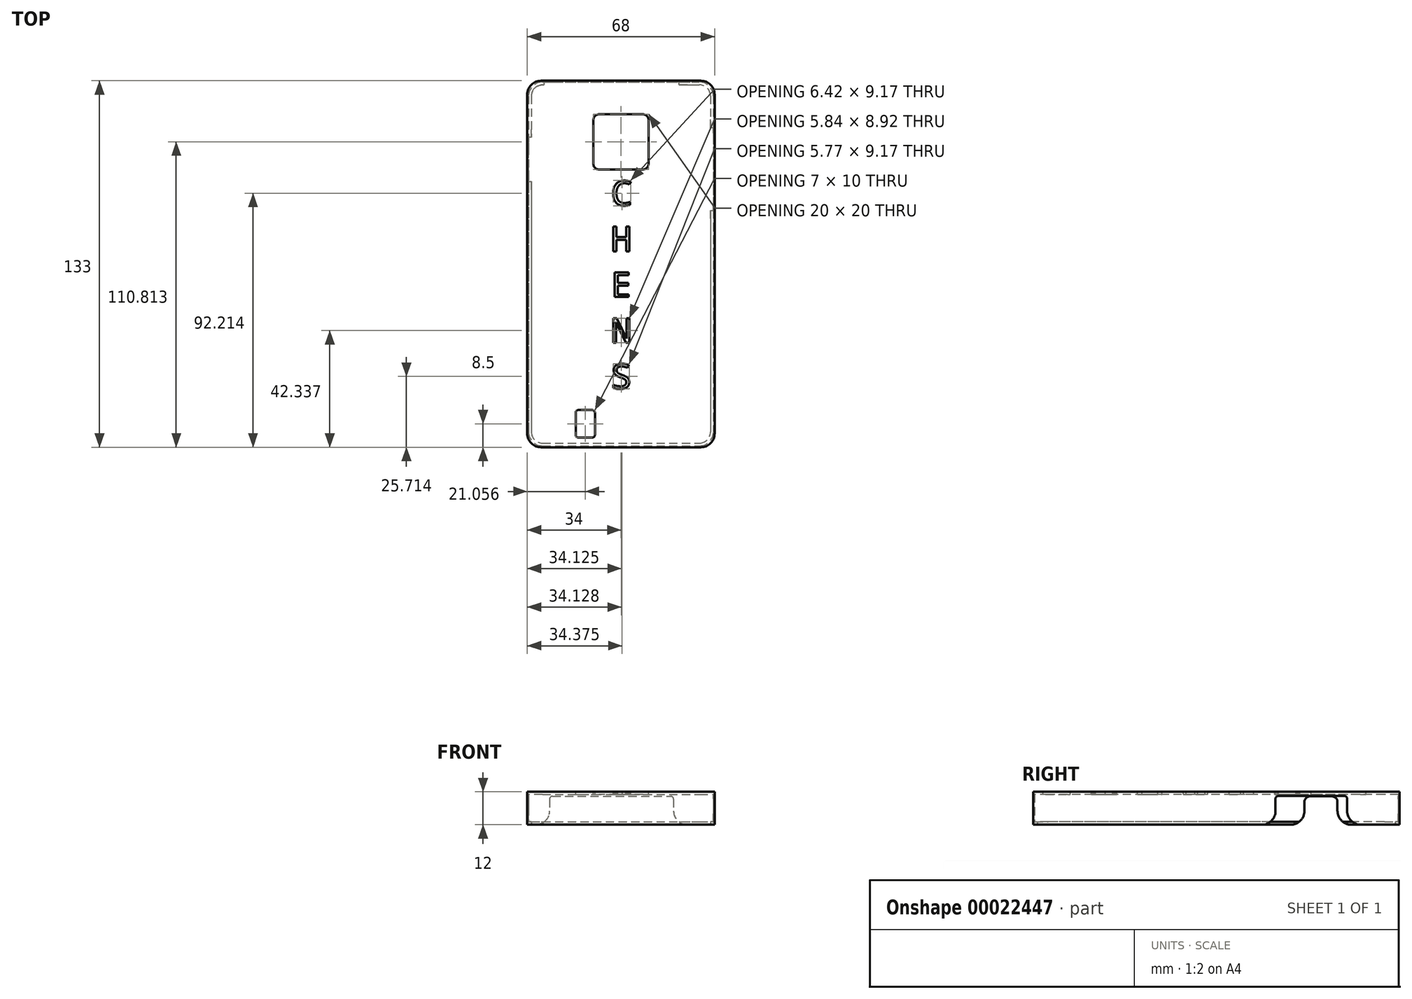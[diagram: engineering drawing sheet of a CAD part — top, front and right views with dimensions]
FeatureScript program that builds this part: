
annotation { "Feature Type Name" : "Feature", "Feature Type Description" : "" }
export const myFeature = defineFeature(function(context is Context, id is Id, definition is map)
    precondition{}
    {
        {
            var Q0;
            Q0=qCreatedBy(makeId("Top.planeOp"),FACE);
            var sketch = newSketch(context, id + "F0", { "sketchPlane" : qUnion([Q0])});
            skLineSegment(sketch, "E0.rect.bottom", {"start": v(29, -66.5) * mm, "end": v(-29, -66.5) * mm});
            skLineSegment(sketch, "E0.rect.top", {"start": v(29, 66.5) * mm, "end": v(-29, 66.5) * mm});
            skLineSegment(sketch, "E0.rect.left", {"start": v(34, -61.5) * mm, "end": v(34, 61.5) * mm});
            skLineSegment(sketch, "E0.rect.right", {"start": v(-34, -61.5) * mm, "end": v(-34, 61.5) * mm});
            skPoint(sketch, "E0.rect.middle", {"position": v(0, 0) * mm});
            skPoint(sketch, "E1.visualSharp", {"position": v(-34, 66.5) * mm});
            skArc(sketch, "E1.filletArc", {"start": v(-29, 66.5) * mm, "mid": v(-32.54, 65.04) * mm, "end": v(-34, 61.5) * mm});
            skPoint(sketch, "E2.visualSharp", {"position": v(-34, -66.5) * mm});
            skArc(sketch, "E2.filletArc", {"start": v(-34, -61.5) * mm, "mid": v(-32.54, -65.04) * mm, "end": v(-29, -66.5) * mm});
            skPoint(sketch, "E3.visualSharp", {"position": v(34, -66.5) * mm});
            skArc(sketch, "E3.filletArc", {"start": v(29, -66.5) * mm, "mid": v(32.54, -65.04) * mm, "end": v(34, -61.5) * mm});
            skPoint(sketch, "E4.visualSharp", {"position": v(34, 66.5) * mm});
            skArc(sketch, "E4.filletArc", {"start": v(34, 61.5) * mm, "mid": v(32.54, 65.04) * mm, "end": v(29, 66.5) * mm});
            skLineSegment(sketch, "E5", {"start": v(0, -66.5) * mm, "end": v(0, 35.5) * mm, "construction": true});
            skLineSegment(sketch, "E6", {"start": v(-34, 44.31) * mm, "end": v(-6.5, 44.31) * mm, "construction": true});
            skLineSegment(sketch, "E7.rect.bottom", {"start": v(8, 54.31) * mm, "end": v(-8, 54.31) * mm});
            skLineSegment(sketch, "E7.rect.top", {"start": v(8, 34.31) * mm, "end": v(-8, 34.31) * mm});
            skLineSegment(sketch, "E7.rect.left", {"start": v(10, 52.31) * mm, "end": v(10, 36.31) * mm});
            skLineSegment(sketch, "E7.rect.right", {"start": v(-10, 52.31) * mm, "end": v(-10, 36.31) * mm});
            skPoint(sketch, "E7.rect.middle", {"position": v(0, 44.31) * mm});
            skPoint(sketch, "E8.visualSharp", {"position": v(-10, 54.31) * mm});
            skArc(sketch, "E8.filletArc", {"start": v(-8, 54.31) * mm, "mid": v(-9.41, 53.73) * mm, "end": v(-10, 52.31) * mm});
            skPoint(sketch, "E9.visualSharp", {"position": v(-10, 34.31) * mm});
            skArc(sketch, "E9.filletArc", {"start": v(-10, 36.31) * mm, "mid": v(-9.41, 34.9) * mm, "end": v(-8, 34.31) * mm});
            skPoint(sketch, "E10.visualSharp", {"position": v(10, 54.31) * mm});
            skArc(sketch, "E10.filletArc", {"start": v(10, 52.31) * mm, "mid": v(9.41, 53.73) * mm, "end": v(8, 54.31) * mm});
            skPoint(sketch, "E11.visualSharp", {"position": v(10, 34.31) * mm});
            skArc(sketch, "E11.filletArc", {"start": v(8, 34.31) * mm, "mid": v(9.41, 34.9) * mm, "end": v(10, 36.31) * mm});
            skLineSegment(sketch, "E12", {"start": v(-34, -58.95) * mm, "end": v(-17, -58.95) * mm, "construction": true});
            skLineSegment(sketch, "E13", {"start": v(-17, -66.5) * mm, "end": v(-17, -63) * mm, "construction": true});
            skLineSegment(sketch, "E14.bottom", {"start": v(-15.44, -63) * mm, "end": v(-10.44, -63) * mm});
            skLineSegment(sketch, "E14.top", {"start": v(-15.44, -53) * mm, "end": v(-10.44, -53) * mm});
            skLineSegment(sketch, "E14.left", {"start": v(-16.44, -62) * mm, "end": v(-16.44, -54) * mm});
            skLineSegment(sketch, "E14.right", {"start": v(-9.44, -62) * mm, "end": v(-9.44, -54) * mm});
            skPoint(sketch, "E15.visualSharp", {"position": v(-16.44, -53) * mm});
            skArc(sketch, "E15.filletArc", {"start": v(-15.44, -53) * mm, "mid": v(-16.15, -53.3) * mm, "end": v(-16.44, -54) * mm});
            skPoint(sketch, "E16.visualSharp", {"position": v(-16.44, -63) * mm});
            skArc(sketch, "E16.filletArc", {"start": v(-16.44, -62) * mm, "mid": v(-16.15, -62.7) * mm, "end": v(-15.44, -63) * mm});
            skPoint(sketch, "E17.visualSharp", {"position": v(-9.44, -53) * mm});
            skArc(sketch, "E17.filletArc", {"start": v(-9.44, -54) * mm, "mid": v(-9.74, -53.3) * mm, "end": v(-10.44, -53) * mm});
            skPoint(sketch, "E18.visualSharp", {"position": v(-9.44, -63) * mm});
            skArc(sketch, "E18.filletArc", {"start": v(-10.44, -63) * mm, "mid": v(-9.74, -62.7) * mm, "end": v(-9.44, -62) * mm});
            skText(sketch, "E19", { "text": "C\nH\nE\nN\nS", "fontName": "DroidSansMono.ttf"});
            const initialGuessF0  = {"E19": [-0.00362, 0.02125, 1, 0, 0.009]};
            skSetInitialGuess(sketch, initialGuessF0);
            skSolve(sketch);
        }
        {
            var Q0;
            Q0 = qSketchRegion(id + "F0", true);
            extrude(context, id + "F1", {"entities" : qUnion([Q0]), "oppositeDirection" : true, "depth" : 11 * mm});
        }
        {
            var Q0;
            Q0=makeQuery(id+"F1.opExtrude","CAP_FACE",FACE,{"disambiguationData":[OSD([sQuery(id+"F0.wireOp",EDGE,"E0.rect.bottom"),sQuery(id+"F0.wireOp",EDGE,"E0.rect.top"),sQuery(id+"F0.wireOp",EDGE,"E0.rect.left"),sQuery(id+"F0.wireOp",EDGE,"E0.rect.right"),sQuery(id+"F0.wireOp",EDGE,"E1.filletArc"),sQuery(id+"F0.wireOp",EDGE,"E2.filletArc"),sQuery(id+"F0.wireOp",EDGE,"E3.filletArc"),sQuery(id+"F0.wireOp",EDGE,"E4.filletArc"),sQuery(id+"F0.wireOp",EDGE,"E7.rect.bottom"),sQuery(id+"F0.wireOp",EDGE,"E7.rect.top"),sQuery(id+"F0.wireOp",EDGE,"E7.rect.left"),sQuery(id+"F0.wireOp",EDGE,"E7.rect.right"),sQuery(id+"F0.wireOp",EDGE,"E8.filletArc"),sQuery(id+"F0.wireOp",EDGE,"E9.filletArc"),sQuery(id+"F0.wireOp",EDGE,"E10.filletArc"),sQuery(id+"F0.wireOp",EDGE,"E11.filletArc"),sQuery(id+"F0.wireOp",EDGE,"E14.bottom"),sQuery(id+"F0.wireOp",EDGE,"E14.top"),sQuery(id+"F0.wireOp",EDGE,"E14.left"),sQuery(id+"F0.wireOp",EDGE,"E14.right"),sQuery(id+"F0.wireOp",EDGE,"E15.filletArc"),sQuery(id+"F0.wireOp",EDGE,"E16.filletArc"),sQuery(id+"F0.wireOp",EDGE,"E17.filletArc"),sQuery(id+"F0.wireOp",EDGE,"E18.filletArc"),sQuery(id+"F0.wireOp",EDGE,"E19.sketch_text.stroke-0"),sQuery(id+"F0.wireOp",EDGE,"E19.sketch_text.stroke-1"),sQuery(id+"F0.wireOp",EDGE,"E19.sketch_text.stroke-2"),sQuery(id+"F0.wireOp",EDGE,"E19.sketch_text.stroke-3"),sQuery(id+"F0.wireOp",EDGE,"E19.sketch_text.stroke-4"),sQuery(id+"F0.wireOp",EDGE,"E19.sketch_text.stroke-5"),sQuery(id+"F0.wireOp",EDGE,"E19.sketch_text.stroke-6"),sQuery(id+"F0.wireOp",EDGE,"E19.sketch_text.stroke-7"),sQuery(id+"F0.wireOp",EDGE,"E19.sketch_text.stroke-8"),sQuery(id+"F0.wireOp",EDGE,"E19.sketch_text.stroke-9"),sQuery(id+"F0.wireOp",EDGE,"E19.sketch_text.stroke-10"),sQuery(id+"F0.wireOp",EDGE,"E19.sketch_text.stroke-11"),sQuery(id+"F0.wireOp",EDGE,"E19.sketch_text.stroke-12"),sQuery(id+"F0.wireOp",EDGE,"E19.sketch_text.stroke-13"),sQuery(id+"F0.wireOp",EDGE,"E19.sketch_text.stroke-14"),sQuery(id+"F0.wireOp",EDGE,"E19.sketch_text.stroke-15"),sQuery(id+"F0.wireOp",EDGE,"E19.sketch_text.stroke-16"),sQuery(id+"F0.wireOp",EDGE,"E19.sketch_text.stroke-17"),sQuery(id+"F0.wireOp",EDGE,"E19.sketch_text.stroke-18"),sQuery(id+"F0.wireOp",EDGE,"E19.sketch_text.stroke-19"),sQuery(id+"F0.wireOp",EDGE,"E19.sketch_text.stroke-20"),sQuery(id+"F0.wireOp",EDGE,"E19.sketch_text.stroke-21"),sQuery(id+"F0.wireOp",EDGE,"E19.sketch_text.stroke-22"),sQuery(id+"F0.wireOp",EDGE,"E19.sketch_text.stroke-23"),sQuery(id+"F0.wireOp",EDGE,"E19.sketch_text.stroke-24"),sQuery(id+"F0.wireOp",EDGE,"E19.sketch_text.stroke-25"),sQuery(id+"F0.wireOp",EDGE,"E19.sketch_text.stroke-26"),sQuery(id+"F0.wireOp",EDGE,"E19.sketch_text.stroke-27"),sQuery(id+"F0.wireOp",EDGE,"E19.sketch_text.stroke-28"),sQuery(id+"F0.wireOp",EDGE,"E19.sketch_text.stroke-29"),sQuery(id+"F0.wireOp",EDGE,"E19.sketch_text.stroke-30"),sQuery(id+"F0.wireOp",EDGE,"E19.sketch_text.stroke-31"),sQuery(id+"F0.wireOp",EDGE,"E19.sketch_text.stroke-32"),sQuery(id+"F0.wireOp",EDGE,"E19.sketch_text.stroke-33"),sQuery(id+"F0.wireOp",EDGE,"E19.sketch_text.stroke-34"),sQuery(id+"F0.wireOp",EDGE,"E19.sketch_text.stroke-35"),sQuery(id+"F0.wireOp",EDGE,"E19.sketch_text.stroke-36"),sQuery(id+"F0.wireOp",EDGE,"E19.sketch_text.stroke-37"),sQuery(id+"F0.wireOp",EDGE,"E19.sketch_text.stroke-38"),sQuery(id+"F0.wireOp",EDGE,"E19.sketch_text.stroke-39"),sQuery(id+"F0.wireOp",EDGE,"E19.sketch_text.stroke-40"),sQuery(id+"F0.wireOp",EDGE,"E19.sketch_text.stroke-41"),sQuery(id+"F0.wireOp",EDGE,"E19.sketch_text.stroke-42"),sQuery(id+"F0.wireOp",EDGE,"E19.sketch_text.stroke-43"),sQuery(id+"F0.wireOp",EDGE,"E19.sketch_text.stroke-44"),sQuery(id+"F0.wireOp",EDGE,"E19.sketch_text.stroke-45"),sQuery(id+"F0.wireOp",EDGE,"E19.sketch_text.stroke-46"),sQuery(id+"F0.wireOp",EDGE,"E19.sketch_text.stroke-47"),sQuery(id+"F0.wireOp",EDGE,"E19.sketch_text.stroke-48"),sQuery(id+"F0.wireOp",EDGE,"E19.sketch_text.stroke-49"),sQuery(id+"F0.wireOp",EDGE,"E19.sketch_text.stroke-50"),sQuery(id+"F0.wireOp",EDGE,"E19.sketch_text.stroke-51"),sQuery(id+"F0.wireOp",EDGE,"E19.sketch_text.stroke-52"),sQuery(id+"F0.wireOp",EDGE,"E19.sketch_text.stroke-53"),sQuery(id+"F0.wireOp",EDGE,"E19.sketch_text.stroke-54"),sQuery(id+"F0.wireOp",EDGE,"E19.sketch_text.stroke-55"),sQuery(id+"F0.wireOp",EDGE,"E19.sketch_text.stroke-56"),sQuery(id+"F0.wireOp",EDGE,"E19.sketch_text.stroke-57"),sQuery(id+"F0.wireOp",EDGE,"E19.sketch_text.stroke-58"),sQuery(id+"F0.wireOp",EDGE,"E19.sketch_text.stroke-59"),sQuery(id+"F0.wireOp",EDGE,"E19.sketch_text.stroke-60"),sQuery(id+"F0.wireOp",EDGE,"E19.sketch_text.stroke-61"),sQuery(id+"F0.wireOp",EDGE,"E19.sketch_text.stroke-62"),sQuery(id+"F0.wireOp",EDGE,"E19.sketch_text.stroke-63"),sQuery(id+"F0.wireOp",EDGE,"E19.sketch_text.stroke-64"),sQuery(id+"F0.wireOp",EDGE,"E19.sketch_text.stroke-65"),sQuery(id+"F0.wireOp",EDGE,"E19.sketch_text.stroke-66"),sQuery(id+"F0.wireOp",EDGE,"E19.sketch_text.stroke-67"),sQuery(id+"F0.wireOp",EDGE,"E19.sketch_text.stroke-68"),sQuery(id+"F0.wireOp",EDGE,"E19.sketch_text.stroke-69"),sQuery(id+"F0.wireOp",EDGE,"E19.sketch_text.stroke-70"),sQuery(id+"F0.wireOp",EDGE,"E19.sketch_text.stroke-71")])],"isStart":false});
            var sketch = newSketch(context, id + "F2", { "sketchPlane" : qUnion([Q0])});
            skLineSegment(sketch, "E20.rect.bottom", {"start": v(-28.5, -66) * mm, "end": v(28.5, -66) * mm});
            skLineSegment(sketch, "E20.rect.top", {"start": v(-28.5, 66) * mm, "end": v(28.5, 66) * mm});
            skLineSegment(sketch, "E20.rect.left", {"start": v(-33.5, -61) * mm, "end": v(-33.5, 61) * mm});
            skLineSegment(sketch, "E20.rect.right", {"start": v(33.5, -61) * mm, "end": v(33.5, 61) * mm});
            skPoint(sketch, "E20.rect.middle", {"position": v(0, 0) * mm});
            skPoint(sketch, "E21.visualSharp", {"position": v(-33.5, -66) * mm});
            skArc(sketch, "E21.filletArc", {"start": v(-33.5, -61) * mm, "mid": v(-32.04, -64.54) * mm, "end": v(-28.5, -66) * mm});
            skPoint(sketch, "E22.visualSharp", {"position": v(33.5, -66) * mm});
            skArc(sketch, "E22.filletArc", {"start": v(28.5, -66) * mm, "mid": v(32.04, -64.54) * mm, "end": v(33.5, -61) * mm});
            skPoint(sketch, "E23.visualSharp", {"position": v(33.5, 66) * mm});
            skArc(sketch, "E23.filletArc", {"start": v(33.5, 61) * mm, "mid": v(32.04, 64.54) * mm, "end": v(28.5, 66) * mm});
            skPoint(sketch, "E24.visualSharp", {"position": v(-33.5, 66) * mm});
            skArc(sketch, "E24.filletArc", {"start": v(-28.5, 66) * mm, "mid": v(-32.04, 64.54) * mm, "end": v(-33.5, 61) * mm});
            skSolve(sketch);
        }
        {
            var Q0;
            Q0 = qSketchRegion(id + "F2", true);
            extrude(context, id + "F3", {"entities" : qUnion([Q0]), "operationType" : NewBodyOperationType.REMOVE, "oppositeDirection" : true, "depth" : 10 * mm});
        }
        {
            var Q0;
            Q0=makeQuery(id+"F1.opExtrude","CAP_FACE",FACE,{"disambiguationData":[OSD([sQuery(id+"F0.wireOp",EDGE,"E0.rect.bottom"),sQuery(id+"F0.wireOp",EDGE,"E0.rect.top"),sQuery(id+"F0.wireOp",EDGE,"E0.rect.left"),sQuery(id+"F0.wireOp",EDGE,"E0.rect.right"),sQuery(id+"F0.wireOp",EDGE,"E1.filletArc"),sQuery(id+"F0.wireOp",EDGE,"E2.filletArc"),sQuery(id+"F0.wireOp",EDGE,"E3.filletArc"),sQuery(id+"F0.wireOp",EDGE,"E4.filletArc"),sQuery(id+"F0.wireOp",EDGE,"E7.rect.bottom"),sQuery(id+"F0.wireOp",EDGE,"E7.rect.top"),sQuery(id+"F0.wireOp",EDGE,"E7.rect.left"),sQuery(id+"F0.wireOp",EDGE,"E7.rect.right"),sQuery(id+"F0.wireOp",EDGE,"E8.filletArc"),sQuery(id+"F0.wireOp",EDGE,"E9.filletArc"),sQuery(id+"F0.wireOp",EDGE,"E10.filletArc"),sQuery(id+"F0.wireOp",EDGE,"E11.filletArc"),sQuery(id+"F0.wireOp",EDGE,"E14.bottom"),sQuery(id+"F0.wireOp",EDGE,"E14.top"),sQuery(id+"F0.wireOp",EDGE,"E14.left"),sQuery(id+"F0.wireOp",EDGE,"E14.right"),sQuery(id+"F0.wireOp",EDGE,"E15.filletArc"),sQuery(id+"F0.wireOp",EDGE,"E16.filletArc"),sQuery(id+"F0.wireOp",EDGE,"E17.filletArc"),sQuery(id+"F0.wireOp",EDGE,"E18.filletArc"),sQuery(id+"F0.wireOp",EDGE,"E19.sketch_text.stroke-0"),sQuery(id+"F0.wireOp",EDGE,"E19.sketch_text.stroke-1"),sQuery(id+"F0.wireOp",EDGE,"E19.sketch_text.stroke-2"),sQuery(id+"F0.wireOp",EDGE,"E19.sketch_text.stroke-3"),sQuery(id+"F0.wireOp",EDGE,"E19.sketch_text.stroke-4"),sQuery(id+"F0.wireOp",EDGE,"E19.sketch_text.stroke-5"),sQuery(id+"F0.wireOp",EDGE,"E19.sketch_text.stroke-6"),sQuery(id+"F0.wireOp",EDGE,"E19.sketch_text.stroke-7"),sQuery(id+"F0.wireOp",EDGE,"E19.sketch_text.stroke-8"),sQuery(id+"F0.wireOp",EDGE,"E19.sketch_text.stroke-9"),sQuery(id+"F0.wireOp",EDGE,"E19.sketch_text.stroke-10"),sQuery(id+"F0.wireOp",EDGE,"E19.sketch_text.stroke-11"),sQuery(id+"F0.wireOp",EDGE,"E19.sketch_text.stroke-12"),sQuery(id+"F0.wireOp",EDGE,"E19.sketch_text.stroke-13"),sQuery(id+"F0.wireOp",EDGE,"E19.sketch_text.stroke-14"),sQuery(id+"F0.wireOp",EDGE,"E19.sketch_text.stroke-15"),sQuery(id+"F0.wireOp",EDGE,"E19.sketch_text.stroke-16"),sQuery(id+"F0.wireOp",EDGE,"E19.sketch_text.stroke-17"),sQuery(id+"F0.wireOp",EDGE,"E19.sketch_text.stroke-18"),sQuery(id+"F0.wireOp",EDGE,"E19.sketch_text.stroke-19"),sQuery(id+"F0.wireOp",EDGE,"E19.sketch_text.stroke-20"),sQuery(id+"F0.wireOp",EDGE,"E19.sketch_text.stroke-21"),sQuery(id+"F0.wireOp",EDGE,"E19.sketch_text.stroke-22"),sQuery(id+"F0.wireOp",EDGE,"E19.sketch_text.stroke-23"),sQuery(id+"F0.wireOp",EDGE,"E19.sketch_text.stroke-24"),sQuery(id+"F0.wireOp",EDGE,"E19.sketch_text.stroke-25"),sQuery(id+"F0.wireOp",EDGE,"E19.sketch_text.stroke-26"),sQuery(id+"F0.wireOp",EDGE,"E19.sketch_text.stroke-27"),sQuery(id+"F0.wireOp",EDGE,"E19.sketch_text.stroke-28"),sQuery(id+"F0.wireOp",EDGE,"E19.sketch_text.stroke-29"),sQuery(id+"F0.wireOp",EDGE,"E19.sketch_text.stroke-30"),sQuery(id+"F0.wireOp",EDGE,"E19.sketch_text.stroke-31"),sQuery(id+"F0.wireOp",EDGE,"E19.sketch_text.stroke-32"),sQuery(id+"F0.wireOp",EDGE,"E19.sketch_text.stroke-33"),sQuery(id+"F0.wireOp",EDGE,"E19.sketch_text.stroke-34"),sQuery(id+"F0.wireOp",EDGE,"E19.sketch_text.stroke-35"),sQuery(id+"F0.wireOp",EDGE,"E19.sketch_text.stroke-36"),sQuery(id+"F0.wireOp",EDGE,"E19.sketch_text.stroke-37"),sQuery(id+"F0.wireOp",EDGE,"E19.sketch_text.stroke-38"),sQuery(id+"F0.wireOp",EDGE,"E19.sketch_text.stroke-39"),sQuery(id+"F0.wireOp",EDGE,"E19.sketch_text.stroke-40"),sQuery(id+"F0.wireOp",EDGE,"E19.sketch_text.stroke-41"),sQuery(id+"F0.wireOp",EDGE,"E19.sketch_text.stroke-42"),sQuery(id+"F0.wireOp",EDGE,"E19.sketch_text.stroke-43"),sQuery(id+"F0.wireOp",EDGE,"E19.sketch_text.stroke-44"),sQuery(id+"F0.wireOp",EDGE,"E19.sketch_text.stroke-45"),sQuery(id+"F0.wireOp",EDGE,"E19.sketch_text.stroke-46"),sQuery(id+"F0.wireOp",EDGE,"E19.sketch_text.stroke-47"),sQuery(id+"F0.wireOp",EDGE,"E19.sketch_text.stroke-48"),sQuery(id+"F0.wireOp",EDGE,"E19.sketch_text.stroke-49"),sQuery(id+"F0.wireOp",EDGE,"E19.sketch_text.stroke-50"),sQuery(id+"F0.wireOp",EDGE,"E19.sketch_text.stroke-51"),sQuery(id+"F0.wireOp",EDGE,"E19.sketch_text.stroke-52"),sQuery(id+"F0.wireOp",EDGE,"E19.sketch_text.stroke-53"),sQuery(id+"F0.wireOp",EDGE,"E19.sketch_text.stroke-54"),sQuery(id+"F0.wireOp",EDGE,"E19.sketch_text.stroke-55"),sQuery(id+"F0.wireOp",EDGE,"E19.sketch_text.stroke-56"),sQuery(id+"F0.wireOp",EDGE,"E19.sketch_text.stroke-57"),sQuery(id+"F0.wireOp",EDGE,"E19.sketch_text.stroke-58"),sQuery(id+"F0.wireOp",EDGE,"E19.sketch_text.stroke-59"),sQuery(id+"F0.wireOp",EDGE,"E19.sketch_text.stroke-60"),sQuery(id+"F0.wireOp",EDGE,"E19.sketch_text.stroke-61"),sQuery(id+"F0.wireOp",EDGE,"E19.sketch_text.stroke-62"),sQuery(id+"F0.wireOp",EDGE,"E19.sketch_text.stroke-63"),sQuery(id+"F0.wireOp",EDGE,"E19.sketch_text.stroke-64"),sQuery(id+"F0.wireOp",EDGE,"E19.sketch_text.stroke-65"),sQuery(id+"F0.wireOp",EDGE,"E19.sketch_text.stroke-66"),sQuery(id+"F0.wireOp",EDGE,"E19.sketch_text.stroke-67"),sQuery(id+"F0.wireOp",EDGE,"E19.sketch_text.stroke-68"),sQuery(id+"F0.wireOp",EDGE,"E19.sketch_text.stroke-69"),sQuery(id+"F0.wireOp",EDGE,"E19.sketch_text.stroke-70"),sQuery(id+"F0.wireOp",EDGE,"E19.sketch_text.stroke-71")])],"isStart":false});
            var sketch = newSketch(context, id + "F4", { "sketchPlane" : qUnion([Q0])});
            skLineSegment(sketch, "E25.rect.bottom", {"start": v(-29, -66.5) * mm, "end": v(29, -66.5) * mm});
            skLineSegment(sketch, "E25.rect.top", {"start": v(-29, 66.5) * mm, "end": v(29, 66.5) * mm});
            skLineSegment(sketch, "E25.rect.left", {"start": v(-34, -61.5) * mm, "end": v(-34, 61.5) * mm});
            skLineSegment(sketch, "E25.rect.right", {"start": v(34, -61.5) * mm, "end": v(34, 61.5) * mm});
            skPoint(sketch, "E25.rect.middle", {"position": v(0, 0) * mm});
            skPoint(sketch, "E26.visualSharp", {"position": v(-34, -66.5) * mm});
            skArc(sketch, "E26.filletArc", {"start": v(-34, -61.5) * mm, "mid": v(-32.54, -65.04) * mm, "end": v(-29, -66.5) * mm});
            skPoint(sketch, "E27.visualSharp", {"position": v(34, -66.5) * mm});
            skArc(sketch, "E27.filletArc", {"start": v(29, -66.5) * mm, "mid": v(32.54, -65.04) * mm, "end": v(34, -61.5) * mm});
            skPoint(sketch, "E28.visualSharp", {"position": v(34, 66.5) * mm});
            skArc(sketch, "E28.filletArc", {"start": v(34, 61.5) * mm, "mid": v(32.54, 65.04) * mm, "end": v(29, 66.5) * mm});
            skPoint(sketch, "E29.visualSharp", {"position": v(-34, 66.5) * mm});
            skArc(sketch, "E29.filletArc", {"start": v(-29, 66.5) * mm, "mid": v(-32.54, 65.04) * mm, "end": v(-34, 61.5) * mm});
            skSolve(sketch);
        }
        {
            var Q0;
            Q0 = qSketchRegion(id + "F4", true);
            extrude(context, id + "F5", {"entities" : qUnion([Q0]), "operationType" : NewBodyOperationType.ADD, "depth" : 1 * mm});
        }
        {
            var Q0;
            Q0=makeQuery(id+"F5.opExtrude","CAP_FACE",FACE,{"disambiguationData":[OSD([sQuery(id+"F4.wireOp",EDGE,"E25.rect.bottom"),sQuery(id+"F4.wireOp",EDGE,"E25.rect.top"),sQuery(id+"F4.wireOp",EDGE,"E25.rect.left"),sQuery(id+"F4.wireOp",EDGE,"E25.rect.right"),sQuery(id+"F4.wireOp",EDGE,"E26.filletArc"),sQuery(id+"F4.wireOp",EDGE,"E27.filletArc"),sQuery(id+"F4.wireOp",EDGE,"E28.filletArc"),sQuery(id+"F4.wireOp",EDGE,"E29.filletArc")])],"isStart":false});
            var sketch = newSketch(context, id + "F6", { "sketchPlane" : qUnion([Q0])});
            skLineSegment(sketch, "E30.rect.bottom", {"start": v(-28.5, -65) * mm, "end": v(28.5, -65) * mm});
            skLineSegment(sketch, "E30.rect.top", {"start": v(-28.5, 65) * mm, "end": v(28.5, 65) * mm});
            skLineSegment(sketch, "E30.rect.left", {"start": v(-32.5, -61) * mm, "end": v(-32.5, 61) * mm});
            skLineSegment(sketch, "E30.rect.right", {"start": v(32.5, -61) * mm, "end": v(32.5, 61) * mm});
            skPoint(sketch, "E30.rect.middle", {"position": v(0, 0) * mm});
            skPoint(sketch, "E31.visualSharp", {"position": v(-32.5, -65) * mm});
            skArc(sketch, "E31.filletArc", {"start": v(-32.5, -61) * mm, "mid": v(-31.33, -63.83) * mm, "end": v(-28.5, -65) * mm});
            skPoint(sketch, "E32.visualSharp", {"position": v(32.5, -65) * mm});
            skArc(sketch, "E32.filletArc", {"start": v(28.5, -65) * mm, "mid": v(31.33, -63.83) * mm, "end": v(32.5, -61) * mm});
            skPoint(sketch, "E33.visualSharp", {"position": v(32.5, 65) * mm});
            skArc(sketch, "E33.filletArc", {"start": v(32.5, 61) * mm, "mid": v(31.33, 63.83) * mm, "end": v(28.5, 65) * mm});
            skPoint(sketch, "E34.visualSharp", {"position": v(-32.5, 65) * mm});
            skArc(sketch, "E34.filletArc", {"start": v(-28.5, 65) * mm, "mid": v(-31.33, 63.83) * mm, "end": v(-32.5, 61) * mm});
            skSolve(sketch);
        }
        {
            var Q0;
            Q0 = qSketchRegion(id + "F6", true);
            extrude(context, id + "F7", {"entities" : qUnion([Q0]), "operationType" : NewBodyOperationType.REMOVE, "oppositeDirection" : true, "depth" : 1 * mm});
        }
        {
            var Q0;
            Q0=makeQuery(id+"F5.boolean.opBoolean","MERGE",FACE,{"derivedFrom":[makeQuery(id+"F1.opExtrude","SWEPT_FACE",FACE,{"disambiguationData":[OSD([sQuery(id+"F0.wireOp",EDGE,"E0.rect.right")])]}),makeQuery(id+"F5.opExtrude","SWEPT_FACE",FACE,{"disambiguationData":[OSD([sQuery(id+"F4.wireOp",EDGE,"E25.rect.left")])]})]});
            var sketch = newSketch(context, id + "F8", { "sketchPlane" : qUnion([Q0])});
            skPoint(sketch, "E35", {"position": v(-61.5, -12) * mm});
            skLineSegment(sketch, "E36", {"start": v(-61.5, -12) * mm, "end": v(-66.53, -12) * mm, "construction": true});
            skLineSegment(sketch, "E37", {"start": v(-66.53, -12) * mm, "end": v(-66.53, -8.37) * mm, "construction": true});
            skLineSegment(sketch, "E38", {"start": v(-66.53, -8.37) * mm, "end": v(-42.53, -8.37) * mm, "construction": true});
            skLineSegment(sketch, "E39", {"start": v(-42.7, -5.25) * mm, "end": v(-33.7, -5.25) * mm, "construction": true});
            skLineSegment(sketch, "E40.bottom", {"start": v(-43.93, -13.2) * mm, "end": v(-31.93, -13.2) * mm});
            skLineSegment(sketch, "E40.top", {"start": v(-41.93, -1.72) * mm, "end": v(-33.93, -1.72) * mm});
            skLineSegment(sketch, "E40.left", {"start": v(-43.93, -13.2) * mm, "end": v(-43.93, -3.72) * mm});
            skLineSegment(sketch, "E40.right", {"start": v(-31.93, -13.2) * mm, "end": v(-31.93, -3.72) * mm});
            skPoint(sketch, "E41.visualSharp", {"position": v(-43.93, -1.72) * mm});
            skArc(sketch, "E41.filletArc", {"start": v(-41.93, -1.72) * mm, "mid": v(-43.34, -2.3) * mm, "end": v(-43.93, -3.72) * mm});
            skPoint(sketch, "E42.visualSharp", {"position": v(-31.93, -1.72) * mm});
            skArc(sketch, "E42.filletArc", {"start": v(-31.93, -3.72) * mm, "mid": v(-32.51, -2.3) * mm, "end": v(-33.93, -1.72) * mm});
            skSolve(sketch);
        }
        {
            var Q0;
            Q0 = qSketchRegion(id + "F8", true);
            extrude(context, id + "F9", {"entities" : qUnion([Q0]), "operationType" : NewBodyOperationType.REMOVE, "oppositeDirection" : true, "depth" : 2 * mm});
        }
        {
            var Q0;
            Q0=makeQuery(id+"F9.boolean.opBoolean","INTERSECT",EDGE,{"derivedFrom":[makeQuery(id+"F5.opExtrude","CAP_FACE",FACE,{"disambiguationData":[OSD([sQuery(id+"F4.wireOp",EDGE,"E25.rect.bottom"),sQuery(id+"F4.wireOp",EDGE,"E25.rect.top"),sQuery(id+"F4.wireOp",EDGE,"E25.rect.left"),sQuery(id+"F4.wireOp",EDGE,"E25.rect.right"),sQuery(id+"F4.wireOp",EDGE,"E26.filletArc"),sQuery(id+"F4.wireOp",EDGE,"E27.filletArc"),sQuery(id+"F4.wireOp",EDGE,"E28.filletArc"),sQuery(id+"F4.wireOp",EDGE,"E29.filletArc")])],"isStart":false}),makeQuery(id+"F9.opExtrude","SWEPT_FACE",FACE,{"disambiguationData":[OSD([sQuery(id+"F8.wireOp",EDGE,"E40.left")])]})]});
            var Q1;
            Q1=makeQuery(id+"F9.boolean.opBoolean","INTERSECT",EDGE,{"derivedFrom":[makeQuery(id+"F5.opExtrude","CAP_FACE",FACE,{"disambiguationData":[OSD([sQuery(id+"F4.wireOp",EDGE,"E25.rect.bottom"),sQuery(id+"F4.wireOp",EDGE,"E25.rect.top"),sQuery(id+"F4.wireOp",EDGE,"E25.rect.left"),sQuery(id+"F4.wireOp",EDGE,"E25.rect.right"),sQuery(id+"F4.wireOp",EDGE,"E26.filletArc"),sQuery(id+"F4.wireOp",EDGE,"E27.filletArc"),sQuery(id+"F4.wireOp",EDGE,"E28.filletArc"),sQuery(id+"F4.wireOp",EDGE,"E29.filletArc")])],"isStart":false}),makeQuery(id+"F9.opExtrude","SWEPT_FACE",FACE,{"disambiguationData":[OSD([sQuery(id+"F8.wireOp",EDGE,"E40.right")])]})]});
            fillet(context, id + "F10", {"entities" : qUnion([Q0, Q1]), "radius" : 5 * mm, "tangentPropagation" : true, "allowEdgeOverflow" : false});
        }
        {
            var Q0;
            Q0=makeQuery(id+"F5.boolean.opBoolean","MERGE",FACE,{"derivedFrom":[makeQuery(id+"F1.opExtrude","SWEPT_FACE",FACE,{"disambiguationData":[OSD([sQuery(id+"F0.wireOp",EDGE,"E0.rect.left")])]}),makeQuery(id+"F5.opExtrude","SWEPT_FACE",FACE,{"disambiguationData":[OSD([sQuery(id+"F4.wireOp",EDGE,"E25.rect.right")])]})]});
            var sketch = newSketch(context, id + "F11", { "sketchPlane" : qUnion([Q0])});
            skPoint(sketch, "E43", {"position": v(61.5, -6) * mm});
            skLineSegment(sketch, "E44", {"start": v(61.5, -6) * mm, "end": v(66.5, -6) * mm, "construction": true});
            skLineSegment(sketch, "E45", {"start": v(66.5, -6) * mm, "end": v(66.5, -4.15) * mm, "construction": true});
            skLineSegment(sketch, "E46", {"start": v(66.5, -4.15) * mm, "end": v(46.5, -4.15) * mm, "construction": true});
            skLineSegment(sketch, "E47.bottom", {"start": v(46.45, -1.57) * mm, "end": v(22.45, -1.57) * mm});
            skLineSegment(sketch, "E47.top", {"start": v(47.45, -13.62) * mm, "end": v(21.45, -13.62) * mm});
            skLineSegment(sketch, "E47.left", {"start": v(47.45, -2.57) * mm, "end": v(47.45, -13.62) * mm});
            skLineSegment(sketch, "E47.right", {"start": v(21.45, -2.57) * mm, "end": v(21.45, -13.62) * mm});
            skPoint(sketch, "E48.visualSharp", {"position": v(47.45, -1.57) * mm});
            skArc(sketch, "E48.filletArc", {"start": v(47.45, -2.57) * mm, "mid": v(47.16, -1.86) * mm, "end": v(46.45, -1.57) * mm});
            skPoint(sketch, "E49.visualSharp", {"position": v(21.45, -1.57) * mm});
            skArc(sketch, "E49.filletArc", {"start": v(22.45, -1.57) * mm, "mid": v(21.74, -1.86) * mm, "end": v(21.45, -2.57) * mm});
            skSolve(sketch);
        }
        {
            var Q0;
            Q0 = qSketchRegion(id + "F11", true);
            extrude(context, id + "F12", {"entities" : qUnion([Q0]), "operationType" : NewBodyOperationType.REMOVE, "oppositeDirection" : true, "depth" : 2 * mm});
        }
        {
            var Q0;
            Q0=makeQuery(id+"F12.boolean.opBoolean","INTERSECT",EDGE,{"derivedFrom":[makeQuery(id+"F5.opExtrude","CAP_FACE",FACE,{"disambiguationData":[OSD([sQuery(id+"F4.wireOp",EDGE,"E25.rect.bottom"),sQuery(id+"F4.wireOp",EDGE,"E25.rect.top"),sQuery(id+"F4.wireOp",EDGE,"E25.rect.left"),sQuery(id+"F4.wireOp",EDGE,"E25.rect.right"),sQuery(id+"F4.wireOp",EDGE,"E26.filletArc"),sQuery(id+"F4.wireOp",EDGE,"E27.filletArc"),sQuery(id+"F4.wireOp",EDGE,"E28.filletArc"),sQuery(id+"F4.wireOp",EDGE,"E29.filletArc")])],"isStart":false}),makeQuery(id+"F12.opExtrude","SWEPT_FACE",FACE,{"disambiguationData":[OSD([sQuery(id+"F11.wireOp",EDGE,"E47.left")])]})]});
            var Q1;
            Q1=makeQuery(id+"F12.boolean.opBoolean","INTERSECT",EDGE,{"derivedFrom":[makeQuery(id+"F5.opExtrude","CAP_FACE",FACE,{"disambiguationData":[OSD([sQuery(id+"F4.wireOp",EDGE,"E25.rect.bottom"),sQuery(id+"F4.wireOp",EDGE,"E25.rect.top"),sQuery(id+"F4.wireOp",EDGE,"E25.rect.left"),sQuery(id+"F4.wireOp",EDGE,"E25.rect.right"),sQuery(id+"F4.wireOp",EDGE,"E26.filletArc"),sQuery(id+"F4.wireOp",EDGE,"E27.filletArc"),sQuery(id+"F4.wireOp",EDGE,"E28.filletArc"),sQuery(id+"F4.wireOp",EDGE,"E29.filletArc")])],"isStart":false}),makeQuery(id+"F12.opExtrude","SWEPT_FACE",FACE,{"disambiguationData":[OSD([sQuery(id+"F11.wireOp",EDGE,"E47.right")])]})]});
            fillet(context, id + "F13", {"entities" : qUnion([Q0, Q1]), "radius" : 5 * mm, "tangentPropagation" : true, "allowEdgeOverflow" : false});
        }
        {
            var Q0;
            Q0=makeQuery(id+"F5.boolean.opBoolean","MERGE",FACE,{"derivedFrom":[makeQuery(id+"F1.opExtrude","SWEPT_FACE",FACE,{"disambiguationData":[OSD([sQuery(id+"F0.wireOp",EDGE,"E0.rect.top")])]}),makeQuery(id+"F5.opExtrude","SWEPT_FACE",FACE,{"disambiguationData":[OSD([sQuery(id+"F4.wireOp",EDGE,"E25.rect.bottom")])]})]});
            var sketch = newSketch(context, id + "F14", { "sketchPlane" : qUnion([Q0])});
            skPoint(sketch, "E50", {"position": v(-29, -6) * mm});
            skPoint(sketch, "E51", {"position": v(29, -6) * mm});
            skLineSegment(sketch, "E52", {"start": v(29, -6) * mm, "end": v(34, -6.08) * mm, "construction": true});
            skLineSegment(sketch, "E53", {"start": v(34, -6.08) * mm, "end": v(34, -7.9) * mm, "construction": true});
            skLineSegment(sketch, "E54", {"start": v(34, -7.9) * mm, "end": v(25.5, -7.9) * mm, "construction": true});
            skLineSegment(sketch, "E55", {"start": v(-29, -6) * mm, "end": v(-34, -6) * mm, "construction": true});
            skLineSegment(sketch, "E56", {"start": v(-34, -6) * mm, "end": v(-34, -8.67) * mm, "construction": true});
            skLineSegment(sketch, "E57", {"start": v(-34, -8.67) * mm, "end": v(-18.5, -8.67) * mm, "construction": true});
            skLineSegment(sketch, "E58.bottom", {"start": v(24.9, -1.7) * mm, "end": v(-18.1, -1.7) * mm});
            skLineSegment(sketch, "E58.top", {"start": v(25.9, -12.7) * mm, "end": v(-19.1, -12.7) * mm});
            skLineSegment(sketch, "E58.left", {"start": v(25.9, -2.7) * mm, "end": v(25.9, -12.7) * mm});
            skLineSegment(sketch, "E58.right", {"start": v(-19.1, -2.7) * mm, "end": v(-19.1, -12.7) * mm});
            skPoint(sketch, "E59.visualSharp", {"position": v(25.9, -1.7) * mm});
            skArc(sketch, "E59.filletArc", {"start": v(25.9, -2.7) * mm, "mid": v(25.6, -2) * mm, "end": v(24.9, -1.7) * mm});
            skPoint(sketch, "E60.visualSharp", {"position": v(-19.1, -1.7) * mm});
            skArc(sketch, "E60.filletArc", {"start": v(-18.1, -1.7) * mm, "mid": v(-18.8, -2) * mm, "end": v(-19.1, -2.7) * mm});
            skSolve(sketch);
        }
        {
            var Q0;
            Q0 = qSketchRegion(id + "F14", true);
            extrude(context, id + "F15", {"entities" : qUnion([Q0]), "operationType" : NewBodyOperationType.REMOVE, "oppositeDirection" : true, "depth" : 2 * mm});
        }
        {
            var Q0;
            {var subQ0=sQuery(id+"F4.wireOp",EDGE,"E25.rect.bottom");var subQ1=sQuery(id+"F4.wireOp",EDGE,"E25.rect.top");var subQ2=sQuery(id+"F4.wireOp",EDGE,"E25.rect.left");var subQ3=sQuery(id+"F4.wireOp",EDGE,"E25.rect.right");var subQ4=sQuery(id+"F4.wireOp",EDGE,"E26.filletArc");var subQ5=sQuery(id+"F4.wireOp",EDGE,"E27.filletArc");var subQ6=sQuery(id+"F4.wireOp",EDGE,"E28.filletArc");var subQ7=sQuery(id+"F4.wireOp",EDGE,"E29.filletArc");Q0=makeQuery(id+"F15.boolean.opBoolean","INTERSECT",EDGE,{"derivedFrom":[makeQuery(id+"F12.boolean.opBoolean","SPLIT",FACE,{"disambiguationData":[TD([makeQuery(id+"F1.opExtrude","SWEPT_FACE",FACE,{"disambiguationData":[OSD([sQuery(id+"F0.wireOp",EDGE,"E0.rect.top")])]})])],"derivedFrom":makeQuery(id+"F5.opExtrude","CAP_FACE",FACE,{"disambiguationData":[OSD([subQ0,subQ1,subQ2,subQ3,subQ4,subQ5,subQ6,subQ7])],"isStart":false})}),makeQuery(id+"F15.opExtrude","SWEPT_FACE",FACE,{"disambiguationData":[OSD([sQuery(id+"F14.wireOp",EDGE,"E58.left")])]})]});}
            var Q1;
            {var subQ0=sQuery(id+"F4.wireOp",EDGE,"E25.rect.bottom");var subQ1=sQuery(id+"F4.wireOp",EDGE,"E25.rect.top");var subQ2=sQuery(id+"F4.wireOp",EDGE,"E25.rect.left");var subQ3=sQuery(id+"F4.wireOp",EDGE,"E25.rect.right");var subQ4=sQuery(id+"F4.wireOp",EDGE,"E26.filletArc");var subQ5=sQuery(id+"F4.wireOp",EDGE,"E27.filletArc");var subQ6=sQuery(id+"F4.wireOp",EDGE,"E28.filletArc");var subQ7=sQuery(id+"F4.wireOp",EDGE,"E29.filletArc");Q1=makeQuery(id+"F15.boolean.opBoolean","INTERSECT",EDGE,{"derivedFrom":[makeQuery(id+"F12.boolean.opBoolean","SPLIT",FACE,{"disambiguationData":[TD([makeQuery(id+"F1.opExtrude","SWEPT_FACE",FACE,{"disambiguationData":[OSD([sQuery(id+"F0.wireOp",EDGE,"E0.rect.top")])]})])],"derivedFrom":makeQuery(id+"F5.opExtrude","CAP_FACE",FACE,{"disambiguationData":[OSD([subQ0,subQ1,subQ2,subQ3,subQ4,subQ5,subQ6,subQ7])],"isStart":false})}),makeQuery(id+"F15.opExtrude","SWEPT_FACE",FACE,{"disambiguationData":[OSD([sQuery(id+"F14.wireOp",EDGE,"E58.right")])]})]});}
            fillet(context, id + "F16", {"entities" : qUnion([Q0, Q1]), "radius" : 5 * mm, "tangentPropagation" : true, "allowEdgeOverflow" : false});
        }
    });
